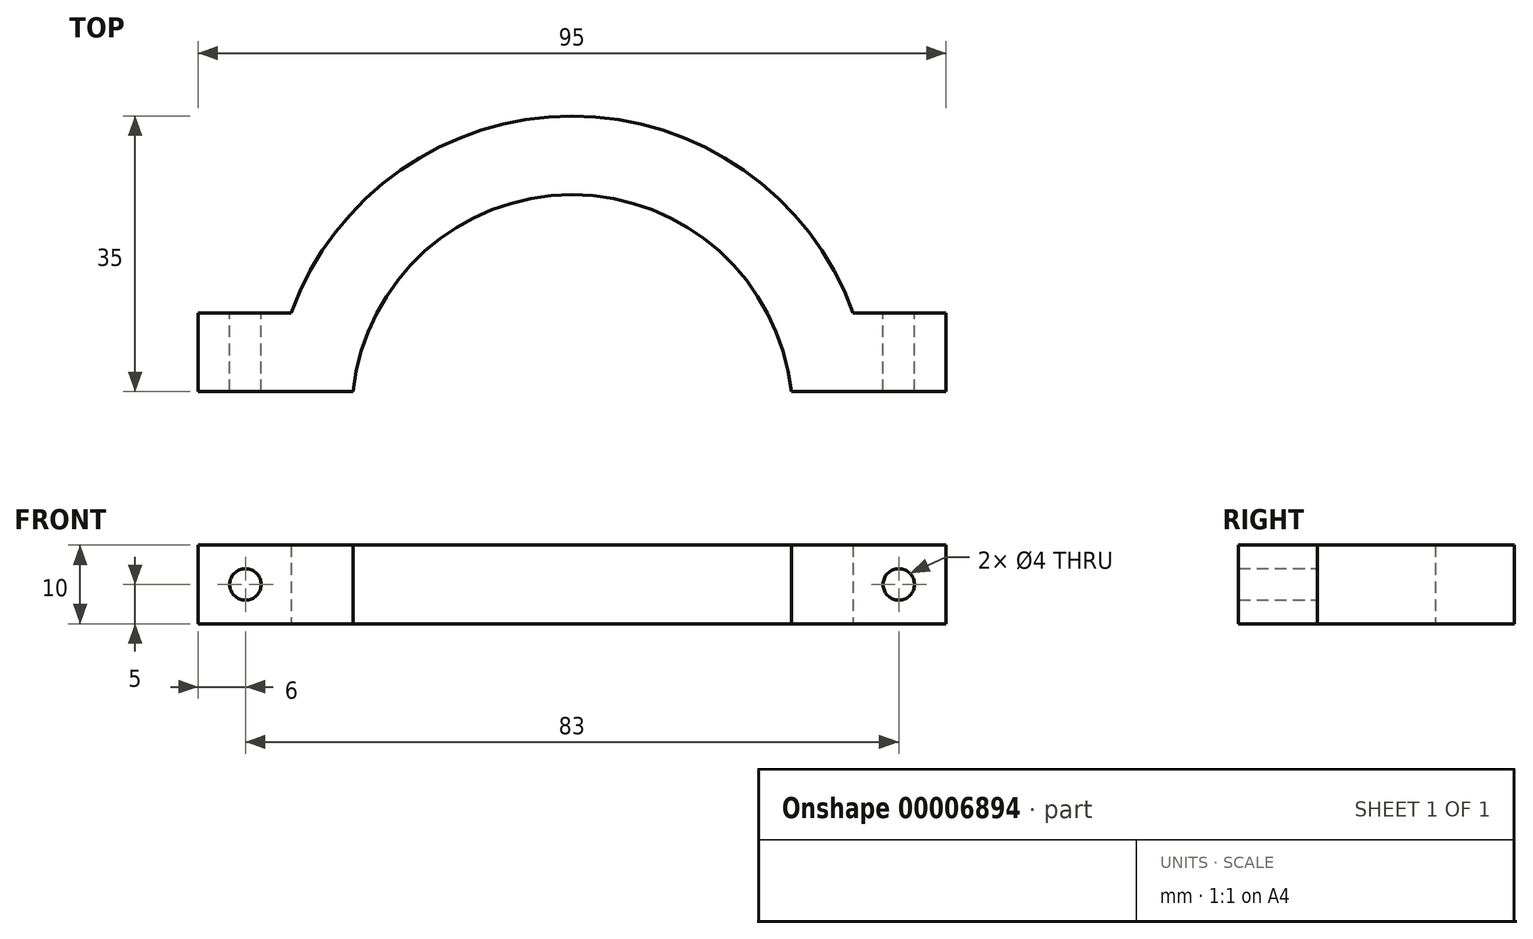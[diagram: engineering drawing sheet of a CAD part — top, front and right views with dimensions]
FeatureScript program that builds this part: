
annotation { "Feature Type Name" : "Feature", "Feature Type Description" : "" }
export const myFeature = defineFeature(function(context is Context, id is Id, definition is map)
    precondition{}
    {
        {
            var Q0;
            Q0=qCreatedBy(makeId("Top.planeOp"),FACE);
            var sketch = newSketch(context, id + "F0", { "sketchPlane" : qUnion([Q0])});
            skArc(sketch, "E0", {"start": v(27.84, 3) * mm, "mid": v(0, 28) * mm, "end": v(-27.84, 3) * mm});
            skLineSegment(sketch, "E1", {"start": v(-47.5, 3) * mm, "end": v(-27.84, 3) * mm});
            skLineSegment(sketch, "E2", {"start": v(47.5, 3) * mm, "end": v(47.5, 13) * mm});
            skLineSegment(sketch, "E3", {"start": v(47.5, 13) * mm, "end": v(35.7, 13) * mm});
            skLineSegment(sketch, "E4", {"start": v(-47.5, 13) * mm, "end": v(-47.5, 3) * mm});
            skArc(sketch, "E5", {"start": v(35.7, 13) * mm, "mid": v(0, 38) * mm, "end": v(-35.7, 13) * mm});
            skLineSegment(sketch, "E6.trimOffspring", {"start": v(-35.7, 13) * mm, "end": v(-47.5, 13) * mm});
            skLineSegment(sketch, "E7.trimOffspring", {"start": v(27.84, 3) * mm, "end": v(47.5, 3) * mm});
            skSolve(sketch);
        }
        {
            var Q0;
            Q0=qSketchRegion(id+"F0",true);
            extrude(context, id + "F1", {"entities" : qUnion([Q0]), "depth" : (10) * mm});
        }
        {
            var Q0;
            Q0=makeQuery(id+"F1.opExtrude","SWEPT_FACE",FACE,{"disambiguationData":[OSD([sQuery(id+"F0.wireOp",EDGE,"E3")])]});
            var sketch = newSketch(context, id + "F2", { "sketchPlane" : qUnion([Q0])});
            skCircle(sketch, "E8", {"center": v(-41.5, 5) * mm, "radius": 2 * mm});
            skLineSegment(sketch, "E9", {"start": v(-47.5, 5) * mm, "end": v(-33.6, 5) * mm, "construction": true});
            skSolve(sketch);
        }
        {
            var Q0;
            Q0=qSketchRegion(id+"F2",true);
            extrude(context, id + "F3", {"entities" : qUnion([Q0]), "operationType" : NewBodyOperationType.REMOVE, "endBound" : BoundingType.THROUGH_ALL, "oppositeDirection" : true, "depth" : 25 * mm});
        }
        {
            var Q0;
            Q0=makeQuery(id+"F1.opExtrude","SWEPT_FACE",FACE,{"disambiguationData":[OSD([sQuery(id+"F0.wireOp",EDGE,"E6.trimOffspring")])]});
            var sketch = newSketch(context, id + "F4", { "sketchPlane" : qUnion([Q0])});
            skLineSegment(sketch, "E10", {"start": v(47.5, 5) * mm, "end": v(35.7, 5) * mm, "construction": true});
            skCircle(sketch, "E11", {"center": v(41.5, 5) * mm, "radius": 2 * mm});
            skSolve(sketch);
        }
        {
            var Q0;
            Q0=qSketchRegion(id+"F4",true);
            extrude(context, id + "F5", {"entities" : qUnion([Q0]), "operationType" : NewBodyOperationType.REMOVE, "endBound" : BoundingType.THROUGH_ALL, "oppositeDirection" : true, "depth" : 25 * mm});
        }
    });
